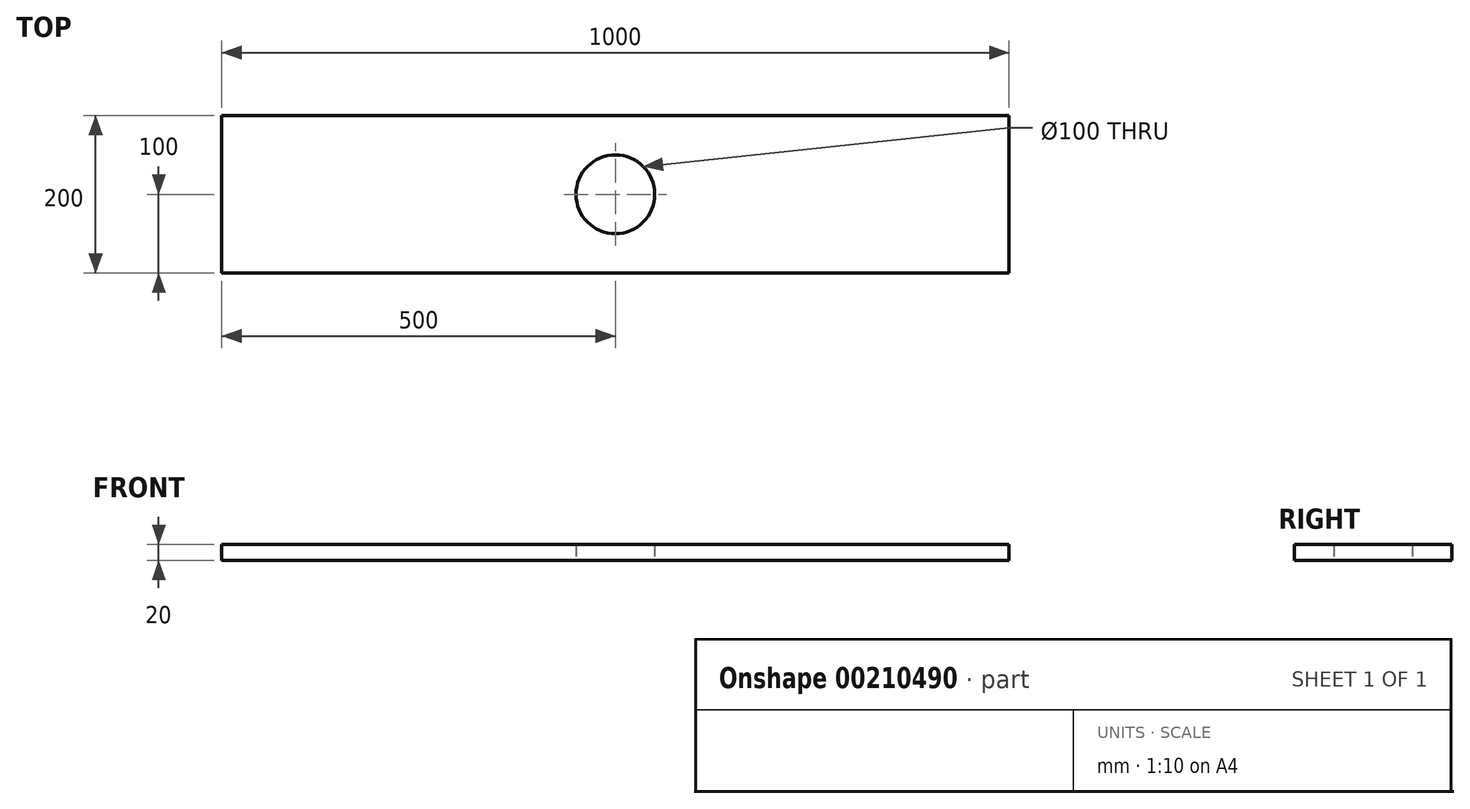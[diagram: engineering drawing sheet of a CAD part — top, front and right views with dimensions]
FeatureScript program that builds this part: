
annotation { "Feature Type Name" : "Feature", "Feature Type Description" : "" }
export const myFeature = defineFeature(function(context is Context, id is Id, definition is map)
    precondition{}
    {
        {
            var Q0;
            Q0=qCreatedBy(makeId("Top.planeOp"),FACE);
            var sketch = newSketch(context, id + "F0", { "sketchPlane" : qUnion([Q0])});
            skLineSegment(sketch, "E0.rect.bottom", {"start": v(-500, 100) * mm, "end": v(500, 100) * mm});
            skLineSegment(sketch, "E0.rect.top", {"start": v(-500, -100) * mm, "end": v(500, -100) * mm});
            skLineSegment(sketch, "E0.rect.left", {"start": v(-500, 100) * mm, "end": v(-500, -100) * mm});
            skLineSegment(sketch, "E0.rect.right", {"start": v(500, 100) * mm, "end": v(500, -100) * mm});
            skPoint(sketch, "E0.rect.middle", {"position": v(0, 0) * mm});
            skCircle(sketch, "E1", {"center": v(0, 0) * mm, "radius": 50 * mm});
            skSolve(sketch);
        }
        {
            var Q0;
            Q0=makeQuery(id+"F0.imprint","IMPRINT",FACE,{"disambiguationData":[TD([[makeQuery(id+"F0.imprint","IMPRINT",EDGE,{"derivedFrom":sQuery(id+"F0.wireOp",EDGE,"E0.rect.bottom")}),-1.0]])]});
            extrude(context, id + "F1", {"entities" : qUnion([Q0]), "depth" : 20 * mm, "symmetric" : true});
        }
    });
